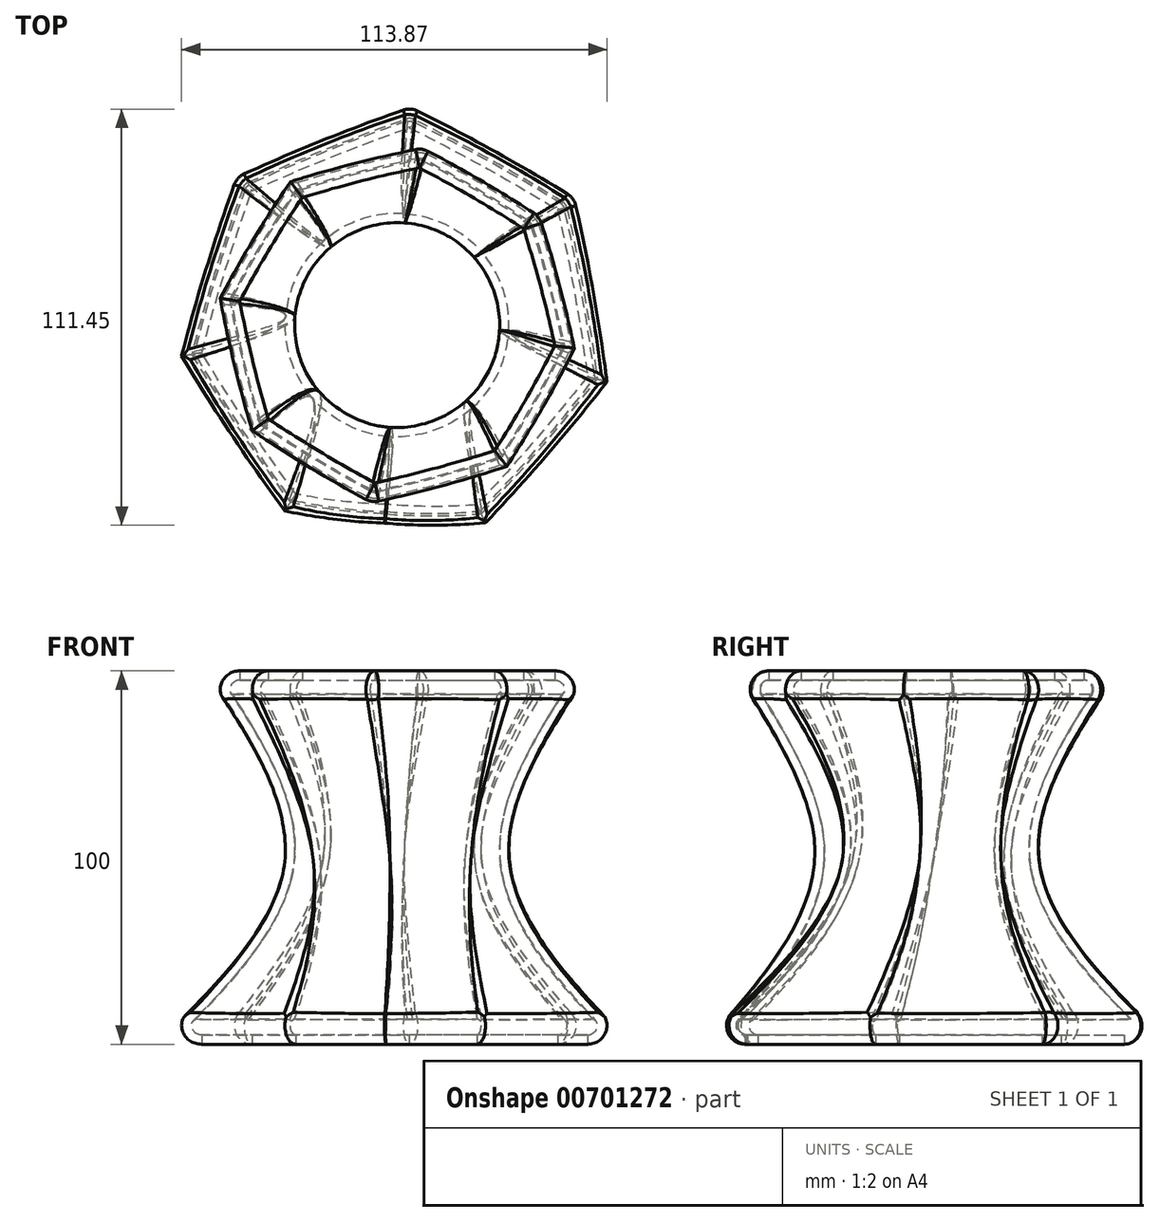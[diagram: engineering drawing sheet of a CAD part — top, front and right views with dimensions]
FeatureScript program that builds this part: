
annotation { "Feature Type Name" : "Feature", "Feature Type Description" : "" }
export const myFeature = defineFeature(function(context is Context, id is Id, definition is map)
    precondition{}
    {
        {
            var Q0;
            Q0=qCreatedBy(makeId("Top.planeOp"),FACE);
            var sketch = newSketch(context, id + "F0", { "sketchPlane" : qUnion([Q0])});
            skCircle(sketch, "E0", {"center": v(0, 0) * mm, "radius": 30 * mm});
            skSolve(sketch);
        }
        {
            var Q0;
            Q0=qCreatedBy(makeId("Top.planeOp"),FACE);
            cPlane(context, id + "F1", {"entities" : qUnion([Q0]), "cplaneType" : CPlaneType.OFFSET, "offset" : 50 * mm, "width" : 150 * mm, "height" : 150 * mm});
        }
        {
            var Q0;
            Q0=qCreatedBy(id+"F1.planeOp",FACE);
            var sketch = newSketch(context, id + "F2", { "sketchPlane" : qUnion([Q0])});
            skCircle(sketch, "E1.cCircle", {"center": v(0, 0) * mm, "radius": 48.34 * mm, "construction": true});
            skLineSegment(sketch, "E1.0", {"start": v(-7.73, -51.75) * mm, "end": v(-42.06, -31.12) * mm});
            skLineSegment(sketch, "E1.1", {"start": v(-42.06, -31.12) * mm, "end": v(-51.75, 7.73) * mm});
            skLineSegment(sketch, "E1.2", {"start": v(-51.75, 7.73) * mm, "end": v(-31.12, 42.06) * mm});
            skLineSegment(sketch, "E1.3", {"start": v(-31.12, 42.06) * mm, "end": v(7.73, 51.75) * mm});
            skLineSegment(sketch, "E1.4", {"start": v(7.73, 51.75) * mm, "end": v(42.06, 31.12) * mm});
            skLineSegment(sketch, "E1.5", {"start": v(42.06, 31.12) * mm, "end": v(51.75, -7.73) * mm});
            skLineSegment(sketch, "E1.6", {"start": v(51.75, -7.73) * mm, "end": v(31.12, -42.06) * mm});
            skLineSegment(sketch, "E1.7", {"start": v(31.12, -42.06) * mm, "end": v(-7.73, -51.75) * mm});
            skPoint(sketch, "E1.0.midPoint", {"position": v(-24.9, -41.44) * mm});
            skSolve(sketch);
        }
        {
            var Q0;
            Q0=qCreatedBy(makeId("Top.planeOp"),FACE);
            cPlane(context, id + "F3", {"entities" : qUnion([Q0]), "cplaneType" : CPlaneType.OFFSET, "offset" : 50 * mm, "oppositeDirection" : true, "width" : 150 * mm, "height" : 150 * mm});
        }
        {
            var Q0;
            Q0=qCreatedBy(id+"F3.planeOp",FACE);
            var sketch = newSketch(context, id + "F4", { "sketchPlane" : qUnion([Q0])});
            skCircle(sketch, "E2.cCircle", {"center": v(0, 0) * mm, "radius": 59.12 * mm, "construction": true});
            skLineSegment(sketch, "E2.0", {"start": v(4.27, 65.48) * mm, "end": v(53.86, 37.49) * mm});
            skLineSegment(sketch, "E2.1", {"start": v(53.86, 37.49) * mm, "end": v(62.9, -18.74) * mm});
            skLineSegment(sketch, "E2.2", {"start": v(62.9, -18.74) * mm, "end": v(24.56, -60.85) * mm});
            skLineSegment(sketch, "E2.3", {"start": v(24.56, -60.85) * mm, "end": v(-32.26, -57.14) * mm});
            skLineSegment(sketch, "E2.4", {"start": v(-32.26, -57.14) * mm, "end": v(-64.8, -10.4) * mm});
            skLineSegment(sketch, "E2.5", {"start": v(-64.8, -10.4) * mm, "end": v(-48.53, 44.17) * mm});
            skLineSegment(sketch, "E2.6", {"start": v(-48.53, 44.17) * mm, "end": v(4.27, 65.48) * mm});
            skPoint(sketch, "E2.0.midPoint", {"position": v(29.07, 51.48) * mm});
            skSolve(sketch);
        }
        {
            var Q0;
            Q0 = qSketchRegion(id + "F4", true);
            var Q1;
            Q1 = qSketchRegion(id + "F0", true);
            var Q2;
            Q2 = qSketchRegion(id + "F2", true);
            loft(context, id + "F5", {"sheetProfilesArray" : [{ "sheetProfileEntities" : qUnion([Q0]) }, { "sheetProfileEntities" : qUnion([Q1]) }, { "sheetProfileEntities" : qUnion([Q2]) }]});
        }
        {
            var Q0;
            Q0=makeQuery(id+"F5.opLoft","CAP_FACE",FACE,{"disambiguationData":[OSD([makeQuery(id+"F4.imprint","IMPRINT",FACE,{"disambiguationData":[TD([[makeQuery(id+"F4.imprint","IMPRINT",EDGE,{"derivedFrom":sQuery(id+"F4.wireOp",EDGE,"E2.0")}),-1.0]])]})])],"isStart":true});
            var Q1;
            Q1=makeQuery(id+"F5.opLoft","MID_CAP_EDGE",EDGE,{"disambiguationData":[OSD([sQuery(id+"F2.wireOp",EDGE,"E1.0"),sQuery(id+"F2.wireOp",EDGE,"E1.1"),sQuery(id+"F2.wireOp",EDGE,"E1.7")])],"capPos":2.0});
            var Q2;
            Q2=makeQuery(id+"F5.opLoft","MID_CAP_EDGE",EDGE,{"disambiguationData":[OSD([sQuery(id+"F2.wireOp",EDGE,"E1.0"),sQuery(id+"F2.wireOp",EDGE,"E1.1"),sQuery(id+"F2.wireOp",EDGE,"E1.2")])],"capPos":2.0});
            var Q3;
            Q3=makeQuery(id+"F5.opLoft","CAP_FACE",FACE,{"disambiguationData":[OSD([makeQuery(id+"F2.imprint","IMPRINT",FACE,{"disambiguationData":[TD([[makeQuery(id+"F2.imprint","IMPRINT",EDGE,{"derivedFrom":sQuery(id+"F2.wireOp",EDGE,"E1.0")}),-1.0]])]})])],"isStart":true});
            fillet(context, id + "F6", {"entities" : qUnion([Q0, Q1, Q2, Q3]), "radius" : 5 * mm, "tangentPropagation" : true, "allowEdgeOverflow" : false});
        }
        {
            var Q0;
            Q0=makeQuery(id+"F5.opLoft","SWEPT_EDGE",EDGE,{"disambiguationData":[OSD([sQuery(id+"F0.wireOp",EDGE,"E0"),sQuery(id+"F2.wireOp",EDGE,"E1.1"),sQuery(id+"F2.wireOp",EDGE,"E1.2"),sQuery(id+"F4.wireOp",EDGE,"E2.4"),sQuery(id+"F4.wireOp",EDGE,"E2.5")])]});
            fillet(context, id + "F7", {"entities" : qUnion([Q0]), "radius" : 5 * mm, "tangentPropagation" : true, "allowEdgeOverflow" : false});
        }
        {
            var Q0;
            Q0=makeQuery(id+"F5.opLoft","SWEPT_EDGE",EDGE,{"disambiguationData":[OSD([sQuery(id+"F0.wireOp",EDGE,"E0"),sQuery(id+"F2.wireOp",EDGE,"E1.0"),sQuery(id+"F2.wireOp",EDGE,"E1.1"),sQuery(id+"F2.wireOp",EDGE,"E1.2")])]});
            var Q1;
            Q1=makeQuery(id+"F5.opLoft","SWEPT_EDGE",EDGE,{"disambiguationData":[OSD([sQuery(id+"F0.wireOp",EDGE,"E0"),sQuery(id+"F2.wireOp",EDGE,"E1.1"),sQuery(id+"F2.wireOp",EDGE,"E1.2"),sQuery(id+"F2.wireOp",EDGE,"E1.3")])]});
            var Q2;
            Q2=makeQuery(id+"F5.opLoft","SWEPT_EDGE",EDGE,{"disambiguationData":[OSD([sQuery(id+"F0.wireOp",EDGE,"E0"),sQuery(id+"F2.wireOp",EDGE,"E1.2"),sQuery(id+"F2.wireOp",EDGE,"E1.3"),sQuery(id+"F4.wireOp",EDGE,"E2.5"),sQuery(id+"F4.wireOp",EDGE,"E2.6")])]});
            var Q3;
            {var subQ0=sQuery(id+"F4.wireOp",EDGE,"E2.6");var subQ1=sQuery(id+"F4.wireOp",EDGE,"E2.5");var subQ2=sQuery(id+"F4.wireOp",EDGE,"E2.4");Q3=makeQuery(id+"F6.opFillet","BLEND_EDGE",EDGE,{"blendedFrom":[makeQuery(id+"F5.opLoft","MID_CAP_EDGE",EDGE,{"disambiguationData":[OSD([subQ2,subQ1,subQ0])],"capPos":0.0}),makeQuery(id+"F5.opLoft","SWEPT_FACE",FACE,{"disambiguationData":[OSD([sQuery(id+"F0.wireOp",EDGE,"E0"),sQuery(id+"F2.wireOp",EDGE,"E1.1"),sQuery(id+"F2.wireOp",EDGE,"E1.2"),sQuery(id+"F2.wireOp",EDGE,"E1.3"),subQ2,subQ1,subQ0])]})],"blendedInto":[makeQuery(id+"F5.opLoft","SWEPT_FACE",FACE,{"disambiguationData":[OSD([sQuery(id+"F0.wireOp",EDGE,"E0"),sQuery(id+"F2.wireOp",EDGE,"E1.1"),sQuery(id+"F2.wireOp",EDGE,"E1.2"),sQuery(id+"F2.wireOp",EDGE,"E1.3"),subQ2,subQ1,subQ0])]})]});}
            var Q4;
            Q4=makeQuery(id+"F5.opLoft","SWEPT_EDGE",EDGE,{"disambiguationData":[OSD([sQuery(id+"F0.wireOp",EDGE,"E0"),sQuery(id+"F2.wireOp",EDGE,"E1.2"),sQuery(id+"F2.wireOp",EDGE,"E1.3"),sQuery(id+"F2.wireOp",EDGE,"E1.4")])]});
            var Q5;
            Q5=makeQuery(id+"F5.opLoft","SWEPT_FACE",FACE,{"disambiguationData":[OSD([sQuery(id+"F0.wireOp",EDGE,"E0"),sQuery(id+"F2.wireOp",EDGE,"E1.2"),sQuery(id+"F2.wireOp",EDGE,"E1.3"),sQuery(id+"F2.wireOp",EDGE,"E1.4"),sQuery(id+"F4.wireOp",EDGE,"E2.5"),sQuery(id+"F4.wireOp",EDGE,"E2.6")])]});
            var Q6;
            Q6=makeQuery(id+"F5.opLoft","SWEPT_FACE",FACE,{"disambiguationData":[OSD([sQuery(id+"F0.wireOp",EDGE,"E0"),sQuery(id+"F2.wireOp",EDGE,"E1.3"),sQuery(id+"F2.wireOp",EDGE,"E1.4"),sQuery(id+"F4.wireOp",EDGE,"E2.0"),sQuery(id+"F4.wireOp",EDGE,"E2.6")])]});
            var Q7;
            Q7=makeQuery(id+"F5.opLoft","SWEPT_EDGE",EDGE,{"disambiguationData":[OSD([sQuery(id+"F0.wireOp",EDGE,"E0"),sQuery(id+"F2.wireOp",EDGE,"E1.5"),sQuery(id+"F2.wireOp",EDGE,"E1.6"),sQuery(id+"F4.wireOp",EDGE,"E2.0"),sQuery(id+"F4.wireOp",EDGE,"E2.1")])]});
            var Q8;
            Q8=makeQuery(id+"F5.opLoft","SWEPT_FACE",FACE,{"disambiguationData":[OSD([sQuery(id+"F0.wireOp",EDGE,"E0"),sQuery(id+"F2.wireOp",EDGE,"E1.5"),sQuery(id+"F2.wireOp",EDGE,"E1.6"),sQuery(id+"F4.wireOp",EDGE,"E2.0"),sQuery(id+"F4.wireOp",EDGE,"E2.1"),sQuery(id+"F4.wireOp",EDGE,"E2.6")])]});
            var Q9;
            Q9=makeQuery(id+"F5.opLoft","SWEPT_EDGE",EDGE,{"disambiguationData":[OSD([sQuery(id+"F0.wireOp",EDGE,"E0"),sQuery(id+"F2.wireOp",EDGE,"E1.4"),sQuery(id+"F2.wireOp",EDGE,"E1.5"),sQuery(id+"F2.wireOp",EDGE,"E1.6")])]});
            var Q10;
            Q10=makeQuery(id+"F5.opLoft","SWEPT_FACE",FACE,{"disambiguationData":[OSD([sQuery(id+"F0.wireOp",EDGE,"E0"),sQuery(id+"F2.wireOp",EDGE,"E1.0"),sQuery(id+"F2.wireOp",EDGE,"E1.6"),sQuery(id+"F2.wireOp",EDGE,"E1.7"),sQuery(id+"F4.wireOp",EDGE,"E2.1"),sQuery(id+"F4.wireOp",EDGE,"E2.2"),sQuery(id+"F4.wireOp",EDGE,"E2.3")])]});
            var Q11;
            Q11=makeQuery(id+"F5.opLoft","SWEPT_FACE",FACE,{"disambiguationData":[OSD([sQuery(id+"F0.wireOp",EDGE,"E0"),sQuery(id+"F2.wireOp",EDGE,"E1.0"),sQuery(id+"F2.wireOp",EDGE,"E1.1"),sQuery(id+"F2.wireOp",EDGE,"E1.7"),sQuery(id+"F4.wireOp",EDGE,"E2.2"),sQuery(id+"F4.wireOp",EDGE,"E2.3"),sQuery(id+"F4.wireOp",EDGE,"E2.4")])]});
            fillet(context, id + "F8", {"entities" : qUnion([Q0, Q1, Q2, Q3, Q4, Q5, Q6, Q7, Q8, Q9, Q10, Q11]), "radius" : 5 * mm, "tangentPropagation" : true, "allowEdgeOverflow" : false});
        }
        {
            var Q0;
            Q0=makeQuery(id+"F5.opLoft","CAP_FACE",FACE,{"disambiguationData":[OSD([makeQuery(id+"F2.imprint","IMPRINT",FACE,{"disambiguationData":[TD([[makeQuery(id+"F2.imprint","IMPRINT",EDGE,{"derivedFrom":sQuery(id+"F2.wireOp",EDGE,"E1.0")}),-1.0]])]})])],"isStart":true});
            var Q1;
            Q1=makeQuery(id+"F5.opLoft","CAP_FACE",FACE,{"disambiguationData":[OSD([makeQuery(id+"F4.imprint","IMPRINT",FACE,{"disambiguationData":[TD([[makeQuery(id+"F4.imprint","IMPRINT",EDGE,{"derivedFrom":sQuery(id+"F4.wireOp",EDGE,"E2.0")}),-1.0]])]})])],"isStart":true});
            shell(context, id + "F9", {"entities" : qUnion([Q0, Q1]), "thickness" : 2.5 * mm});
        }
    });
